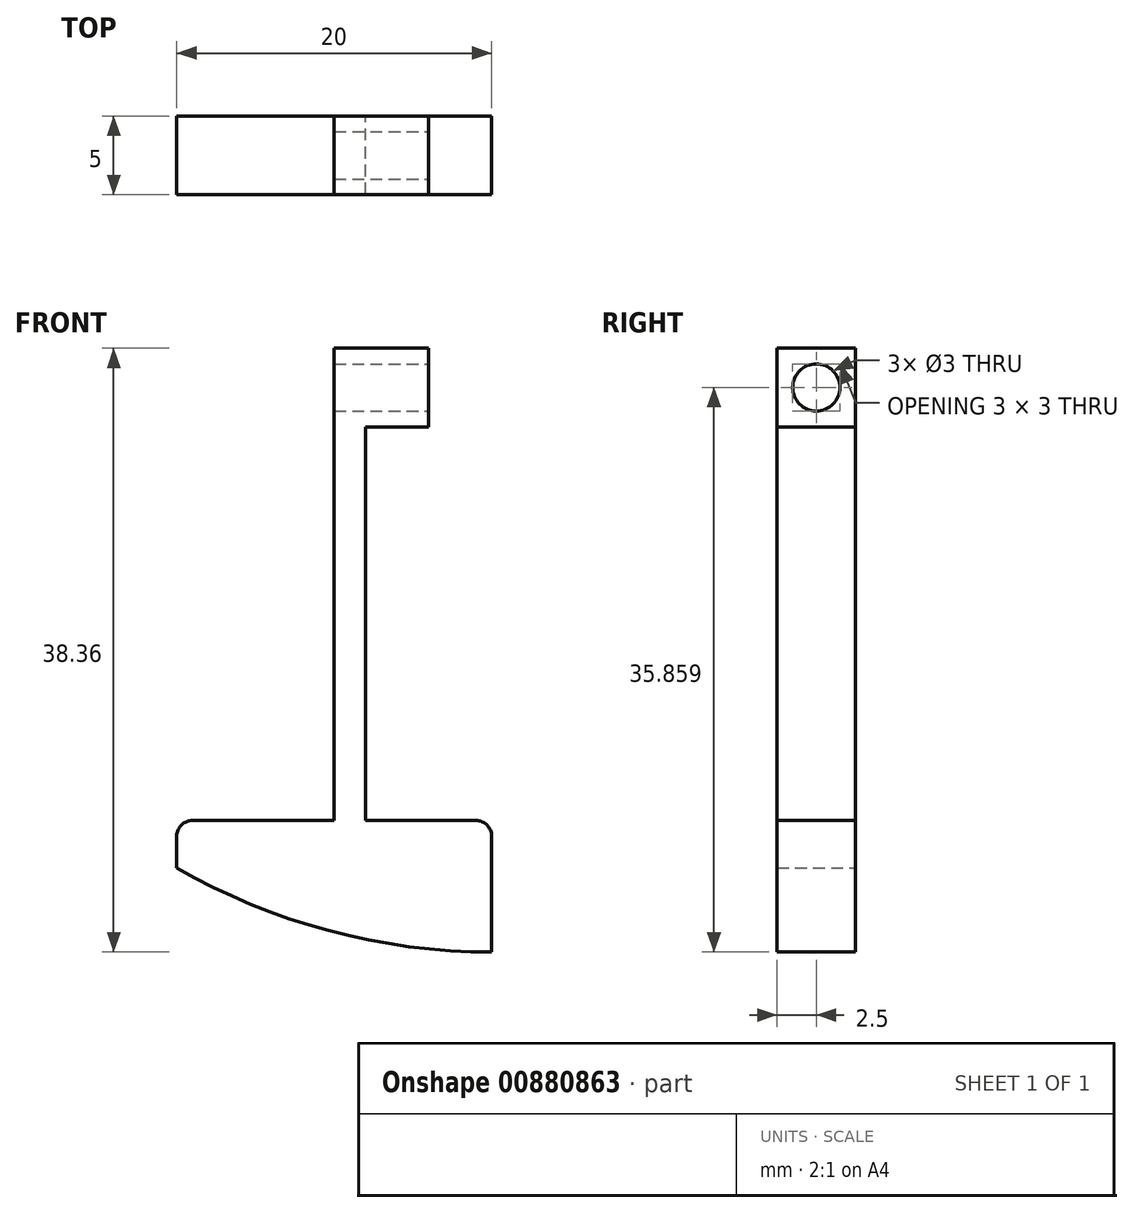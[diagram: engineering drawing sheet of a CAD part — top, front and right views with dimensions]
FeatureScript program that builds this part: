
annotation { "Feature Type Name" : "Feature", "Feature Type Description" : "" }
export const myFeature = defineFeature(function(context is Context, id is Id, definition is map)
    precondition{}
    {
        {
            var Q0;
            Q0=qCreatedBy(makeId("Front.planeOp"),FACE);
            var sketch = newSketch(context, id + "F0", { "sketchPlane" : qUnion([Q0])});
            skArc(sketch, "E0", {"start": v(-20, 5.36) * mm, "mid": v(-10.35, 1.36) * mm, "end": v(0, 0) * mm});
            skLineSegment(sketch, "E1", {"start": v(0, 0) * mm, "end": v(0, 7.36) * mm, "construction": true});
            skLineSegment(sketch, "E2", {"start": v(0, 0) * mm, "end": v(0, 8.36) * mm});
            skLineSegment(sketch, "E3", {"start": v(-1, 8.36) * mm, "end": v(-8, 8.36) * mm});
            skLineSegment(sketch, "E4", {"start": v(-20, 7.36) * mm, "end": v(-20, 5.36) * mm});
            skLineSegment(sketch, "E5", {"start": v(-10, 8.36) * mm, "end": v(-10, 38.36) * mm});
            skLineSegment(sketch, "E6", {"start": v(-10, 38.36) * mm, "end": v(-4, 38.36) * mm});
            skLineSegment(sketch, "E7", {"start": v(-4, 38.36) * mm, "end": v(-4, 33.36) * mm});
            skLineSegment(sketch, "E8", {"start": v(-4, 33.36) * mm, "end": v(-8, 33.36) * mm});
            skLineSegment(sketch, "E9", {"start": v(-8, 33.36) * mm, "end": v(-8, 8.36) * mm});
            skPoint(sketch, "E10.newPointB", {"position": v(0, 8.36) * mm});
            skArc(sketch, "E10.filletArc", {"start": v(0, 7.36) * mm, "mid": v(-0.3, 8.07) * mm, "end": v(-1, 8.36) * mm});
            skPoint(sketch, "E11.visualSharp", {"position": v(-20, 8.36) * mm});
            skArc(sketch, "E11.filletArc", {"start": v(-19, 8.36) * mm, "mid": v(-19.7, 8.07) * mm, "end": v(-20, 7.36) * mm});
            skLineSegment(sketch, "E12.trimOffspring", {"start": v(-10, 8.36) * mm, "end": v(-19, 8.36) * mm});
            skSolve(sketch);
        }
        {
            var Q0;
            Q0 = qSketchRegion(id + "F0", true);
            extrude(context, id + "F1", {"entities" : qUnion([Q0]), "endBound" : BoundingType.SYMMETRIC, "depth" : 5 * mm, "offsetDistance" : 25 * mm});
        }
        {
            var Q0;
            Q0=makeQuery(id+"F1.opExtrude","SWEPT_FACE",FACE,{"disambiguationData":[OSD([sQuery(id+"F0.wireOp",EDGE,"E7")])]});
            var sketch = newSketch(context, id + "F2", { "sketchPlane" : qUnion([Q0])});
            skLineSegment(sketch, "E13", {"start": v(0, 38.36) * mm, "end": v(0, 33.36) * mm, "construction": true});
            skLineSegment(sketch, "E14", {"start": v(-2.5, 35.86) * mm, "end": v(2.5, 35.86) * mm, "construction": true});
            skCircle(sketch, "E15", {"center": v(0, 35.86) * mm, "radius": 1.5 * mm});
            skSolve(sketch);
        }
        {
            var Q0;
            Q0 = qSketchRegion(id + "F2", true);
            extrude(context, id + "F3", {"entities" : qUnion([Q0]), "operationType" : NewBodyOperationType.REMOVE, "endBound" : BoundingType.THROUGH_ALL, "oppositeDirection" : true, "depth" : 25 * mm, "offsetDistance" : 25 * mm});
        }
    });
